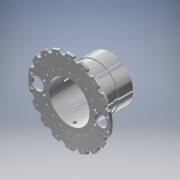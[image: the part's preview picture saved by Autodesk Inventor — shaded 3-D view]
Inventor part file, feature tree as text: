
AUTODESK INVENTOR PART (.ipt)
format: ipt  version: 2016 (Build 200138000, 138)  size: 384,000 bytes
history: native  units: mm
features: sketch x9, extrude x6, hole x5, pattern_circular x3, projected_geometry x3, plane x2, mirror x2, fillet x1
ambient origin geometry x8: Origin, YZ Plane, XZ Plane, XY Plane, X Axis, Y Axis, Z Axis, Center Point
bodies: Solid1 (feature_tree)
feature tree (31):
  sketch  "Sketch1"  dims[d0=151.2mm d1=76.6mm]
  extrude  "Extrusion1"  Depth=76.6mm
  extrude  "Extrusion2"  Depth=3.0mm
  plane  "Work Plane1"
  extrude  "Extrusion3"  Depth=23.0mm
  extrude  "Extrusion4"  Depth=28.3mm
  pattern_circular  "Circular Pattern1"  [2 undecoded]
  fillet  "Fillet1"  Radius=1.5mm
  hole  "Hole1"  [1 undecoded]
  extrude  "Extrusion5"  Depth=6.0mm
  hole  "Hole2"  [1 undecoded]
  hole  "Hole3"  [1 undecoded]
  plane  "Work Plane2"
  hole  "Hole4"  [1 undecoded]
  extrude  "Extrusion6"  Depth=10.0mm TaperAngle=0.0deg
  pattern_circular  "Circular Pattern2"  [2 undecoded]
  mirror  "Mirror2"
  mirror  "Mirror3"
  sketch  "Sketch10"  dims[d12=3.0mm d13=36.0mm d14=1.5mm d15=10.0mm d16=0.0mm d17=0.698132mm d18=48.0mm d19=0.0mm d20=60.0mm d21=360.0deg d23=2.6mm d24=6.0mm d25=4.0mm d26=2.0mm d27=90.0deg d28=8.0mm d29=20.594885mm d30=23.0mm d31=10.0mm d32=0.0mm d33=5.4mm d34=6.0mm d35=4.0mm d36=2.0mm d37=90.0deg d38=3.0mm d39=20.594885mm d40=6.0mm d41=3.0mm d42=40.0mm d44=60.0deg d46=40.0mm d48=60.0deg d50=3.1mm d51=6.0mm d52=4.0mm d53=2.0mm d54=90.0deg d55=8.0mm d56=20.594885mm d57=6.0mm d58=6.0mm d59=6.0mm d60=4.0mm d61=2.0mm d62=90.0deg d63=8.0mm d64=20.594885mm d65=12.0mm d66=1.745329mm d67=10.0mm d68=0.0mm d69=40.0mm d70=60.0deg d74=18.0mm d76=6.5mm d78=9.5mm d79=12.8mm d80=3.3mm d81=4.0mm d82=1.5mm d83=6.5mm d84=2.1mm d85=6.0mm d86=4.0mm d87=2.0mm d88=90.0deg d89=8.0mm d90=20.594885mm d91=20.0mm d92=360.0deg d97=66.0mm d99=50.9mm]
  sketch  "Sketch9"  dims[d11=0.0mm]
  hole  "Hole5"  [1 undecoded]
  pattern_circular  "Circular Pattern3"  [2 undecoded]
  sketch  "Sketch2"  dims[d2=3.0mm d3=74.6mm]
  sketch  "Sketch3"  dims[d4=23.0mm d5=23.0mm]
  sketch  "Sketch4"  dims[d6=28.3mm d7=28.3mm]
  sketch  "Sketch5"  dims[d8=4.5mm]
  projected_geometry  "Projected Loop1"
  sketch  "Sketch6"  dims[d9=0.0mm]
  sketch  "Sketch7"  dims[d10=72.0mm]
  projected_geometry  "Project Cut Edges1"
  projected_geometry  "Project Cut Edges2"
note: 11 required parameter values undecoded (feature->parameter linkage not recoverable at this tier; creation-order binding heuristic only, values carry confidence <= 0.55)
